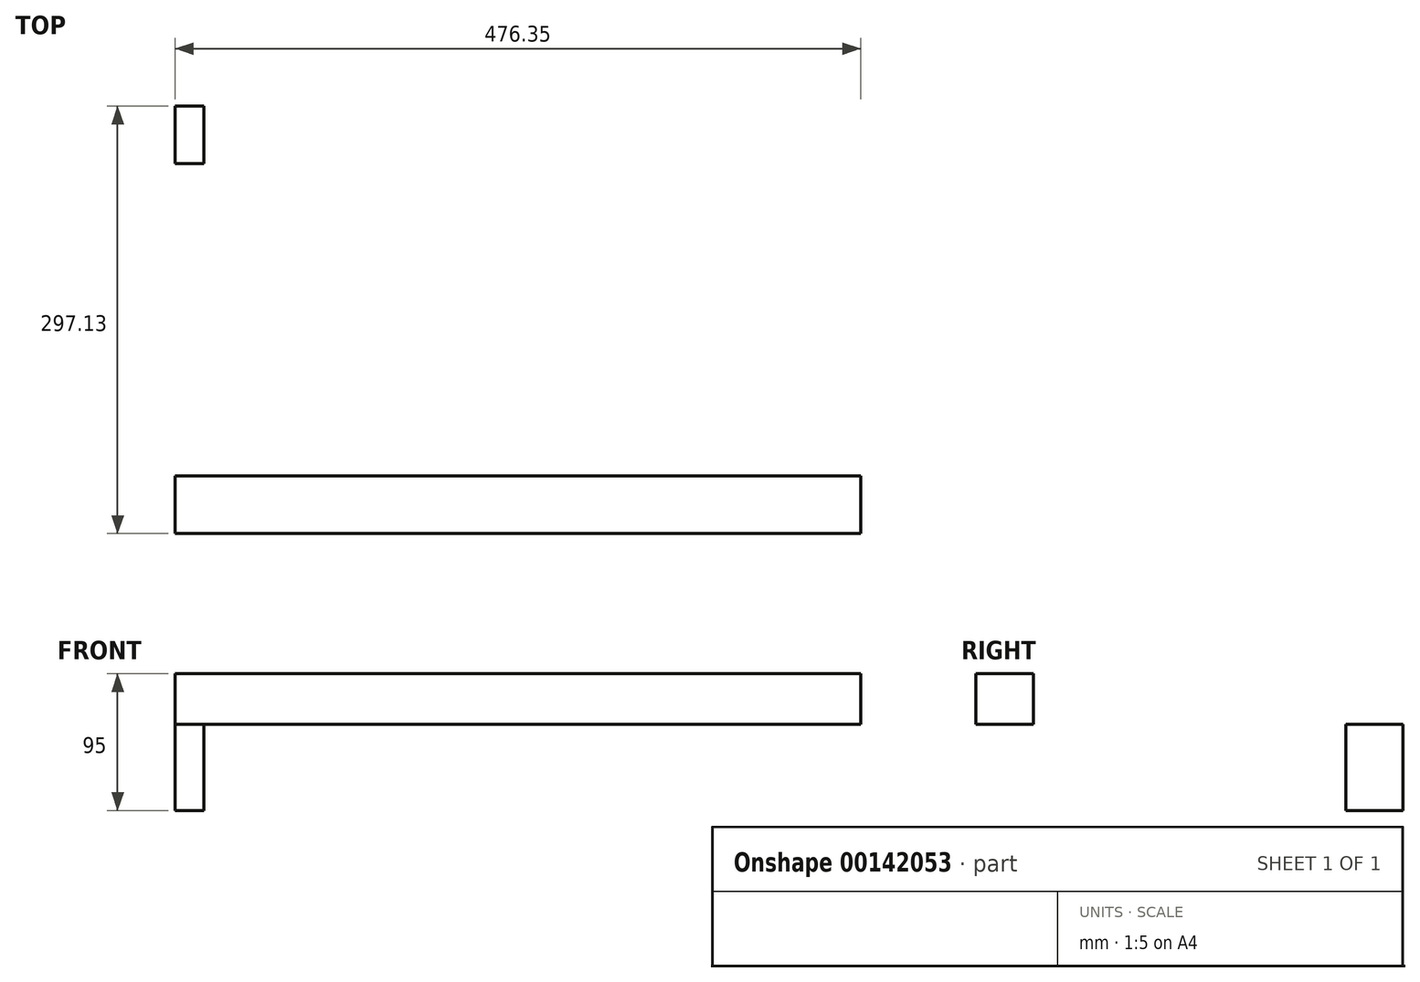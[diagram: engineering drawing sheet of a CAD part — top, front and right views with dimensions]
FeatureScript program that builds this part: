
annotation { "Feature Type Name" : "Feature", "Feature Type Description" : "" }
export const myFeature = defineFeature(function(context is Context, id is Id, definition is map)
    precondition{}
    {
        {
            var Q0;
            Q0=qCreatedBy(makeId("Top.planeOp"),FACE);
            var sketch = newSketch(context, id + "F0", { "sketchPlane" : qUnion([Q0])});
            skLineSegment(sketch, "E0.bottom", {"start": v(-127.44, 57.35) * mm, "end": v(172.56, 57.35) * mm});
            skLineSegment(sketch, "E0.top", {"start": v(-127.44, -142.65) * mm, "end": v(172.56, -142.65) * mm});
            skLineSegment(sketch, "E0.left", {"start": v(-127.44, 57.35) * mm, "end": v(-127.44, -142.65) * mm});
            skLineSegment(sketch, "E0.right", {"start": v(172.56, 57.35) * mm, "end": v(172.56, -142.65) * mm});
            skLineSegment(sketch, "E1.bottom", {"start": v(-236.3, 146.91) * mm, "end": v(253.7, 146.91) * mm});
            skLineSegment(sketch, "E1.top", {"start": v(-236.3, -253.09) * mm, "end": v(253.7, -253.09) * mm});
            skLineSegment(sketch, "E1.left", {"start": v(-236.3, 146.91) * mm, "end": v(-236.3, -253.09) * mm});
            skLineSegment(sketch, "E1.right", {"start": v(253.7, 146.91) * mm, "end": v(253.7, -253.09) * mm});
            skLineSegment(sketch, "E2.bottom", {"start": v(-156.3, 106.91) * mm, "end": v(193.7, 106.91) * mm});
            skLineSegment(sketch, "E2.top", {"start": v(-156.3, -193.09) * mm, "end": v(193.7, -193.09) * mm});
            skLineSegment(sketch, "E2.left", {"start": v(-156.3, 106.91) * mm, "end": v(-156.3, -193.09) * mm});
            skLineSegment(sketch, "E2.right", {"start": v(193.7, 106.91) * mm, "end": v(193.7, -193.09) * mm});
            skLineSegment(sketch, "E3.bottom", {"start": v(253.7, 106.91) * mm, "end": v(233.7, 106.91) * mm});
            skLineSegment(sketch, "E3.top", {"start": v(253.7, -213.09) * mm, "end": v(233.7, -213.09) * mm});
            skLineSegment(sketch, "E3.left", {"start": v(253.7, 106.91) * mm, "end": v(253.7, -213.09) * mm});
            skLineSegment(sketch, "E3.right", {"start": v(233.7, 106.91) * mm, "end": v(233.7, -213.09) * mm});
            skLineSegment(sketch, "E4.bottom", {"start": v(-236.3, 106.91) * mm, "end": v(-196.3, 106.91) * mm});
            skLineSegment(sketch, "E4.top", {"start": v(-236.3, -213.09) * mm, "end": v(-196.3, -213.09) * mm});
            skLineSegment(sketch, "E4.left", {"start": v(-236.3, 106.91) * mm, "end": v(-236.3, -213.09) * mm});
            skLineSegment(sketch, "E4.right", {"start": v(-196.3, 106.91) * mm, "end": v(-196.3, -213.09) * mm});
            skLineSegment(sketch, "E5.bottom", {"start": v(-236.3, -213.09) * mm, "end": v(-216.3, -213.09) * mm});
            skLineSegment(sketch, "E5.top", {"start": v(-236.3, -253.09) * mm, "end": v(-216.3, -253.09) * mm});
            skLineSegment(sketch, "E5.left", {"start": v(-236.3, -213.09) * mm, "end": v(-236.3, -253.09) * mm});
            skLineSegment(sketch, "E5.right", {"start": v(-216.3, -213.09) * mm, "end": v(-216.3, -253.09) * mm});
            skLineSegment(sketch, "E6.bottom", {"start": v(-236.3, 106.91) * mm, "end": v(-216.3, 106.91) * mm});
            skLineSegment(sketch, "E6.top", {"start": v(-236.3, 146.91) * mm, "end": v(-216.3, 146.91) * mm});
            skLineSegment(sketch, "E6.left", {"start": v(-236.3, 106.91) * mm, "end": v(-236.3, 146.91) * mm});
            skLineSegment(sketch, "E6.right", {"start": v(-216.3, 106.91) * mm, "end": v(-216.3, 146.91) * mm});
            skSolve(sketch);
        }
        {
            var Q0;
            {var subQ5=sQuery(id+"F0.wireOp",EDGE,"E1.bottom");Q0=makeQuery(id+"F0.imprint","IMPRINT",FACE,{"disambiguationData":[TD([[makeQuery(id+"F0.imprint","IMPRINT",EDGE,{"derivedFrom":subQ5}),-1.0]])]});}
            extrude(context, id + "F1", {"entities" : qUnion([Q0]), "depth" : 60 * mm});
        }
        {
            var Q0;
            Q0=makeQuery(id+"F1.opExtrude","CAP_FACE",FACE,{"disambiguationData":[OSD([sQuery(id+"F0.wireOp",EDGE,"E1.bottom"),sQuery(id+"F0.wireOp",EDGE,"E1.top"),sQuery(id+"F0.wireOp",EDGE,"E1.right"),sQuery(id+"F0.wireOp",EDGE,"E2.bottom"),sQuery(id+"F0.wireOp",EDGE,"E2.top"),sQuery(id+"F0.wireOp",EDGE,"E2.left"),sQuery(id+"F0.wireOp",EDGE,"E2.right"),sQuery(id+"F0.wireOp",EDGE,"E3.bottom"),sQuery(id+"F0.wireOp",EDGE,"E3.top"),sQuery(id+"F0.wireOp",EDGE,"E3.right"),sQuery(id+"F0.wireOp",EDGE,"E4.bottom"),sQuery(id+"F0.wireOp",EDGE,"E4.top"),sQuery(id+"F0.wireOp",EDGE,"E4.right"),sQuery(id+"F0.wireOp",EDGE,"E5.right"),sQuery(id+"F0.wireOp",EDGE,"E6.right")])],"isStart":false});
            var sketch = newSketch(context, id + "F2", { "sketchPlane" : qUnion([Q0])});
            skLineSegment(sketch, "E7.0.0", {"start": v(253.7, 146.91) * mm, "end": v(-216.3, 146.91) * mm});
            skLineSegment(sketch, "E7.0.1", {"start": v(-216.3, 146.91) * mm, "end": v(-216.3, 106.91) * mm});
            skLineSegment(sketch, "E7.0.2", {"start": v(-216.3, 106.91) * mm, "end": v(-196.3, 106.91) * mm});
            skLineSegment(sketch, "E7.0.3", {"start": v(-196.3, 106.91) * mm, "end": v(-196.3, -213.09) * mm});
            skLineSegment(sketch, "E7.0.4", {"start": v(-196.3, -213.09) * mm, "end": v(-216.3, -213.09) * mm});
            skLineSegment(sketch, "E7.0.5", {"start": v(-216.3, -213.09) * mm, "end": v(-216.3, -253.09) * mm});
            skLineSegment(sketch, "E7.0.6", {"start": v(-216.3, -253.09) * mm, "end": v(253.7, -253.09) * mm});
            skLineSegment(sketch, "E7.0.7", {"start": v(253.7, -253.09) * mm, "end": v(253.7, -213.09) * mm});
            skLineSegment(sketch, "E7.0.8", {"start": v(253.7, -213.09) * mm, "end": v(233.7, -213.09) * mm});
            skLineSegment(sketch, "E7.0.9", {"start": v(233.7, -213.09) * mm, "end": v(233.7, 106.91) * mm});
            skLineSegment(sketch, "E7.0.10", {"start": v(233.7, 106.91) * mm, "end": v(253.7, 106.91) * mm});
            skLineSegment(sketch, "E7.0.11", {"start": v(253.7, 106.91) * mm, "end": v(253.7, 146.91) * mm});
            skLineSegment(sketch, "E8.bottom", {"start": v(-236.3, -110.22) * mm, "end": v(240.05, -110.22) * mm});
            skLineSegment(sketch, "E8.top", {"start": v(-236.3, -150.22) * mm, "end": v(240.05, -150.22) * mm});
            skLineSegment(sketch, "E8.left", {"start": v(-236.3, -110.22) * mm, "end": v(-236.3, -150.22) * mm});
            skLineSegment(sketch, "E8.right", {"start": v(240.05, -110.22) * mm, "end": v(240.05, -150.22) * mm});
            skSolve(sketch);
        }
        {
            var Q0;
            {var subQ5=sQuery(id+"F2.wireOp",EDGE,"E8.left");Q0=makeQuery(id+"F2.imprint","IMPRINT",FACE,{"disambiguationData":[TD([[makeQuery(id+"F2.imprint","IMPRINT",EDGE,{"derivedFrom":subQ5}),1.0]])]});}
            var Q1;
            {var subQ0=sQuery(id+"F2.wireOp",EDGE,"E8.bottom");var subQ1=sQuery(id+"F2.wireOp",EDGE,"E7.0.3");var subQ2=makeQuery(id+"F2.imprint","INTERSECT",VERTEX,{"derivedFrom":[subQ1,subQ0]});Q1=makeQuery(id+"F2.imprint","IMPRINT",FACE,{"disambiguationData":[TD([[makeQuery(id+"F2.imprint","IMPRINT",EDGE,{"disambiguationData":[TD([[subQ2,-1.0]])],"derivedFrom":subQ1}),1.0]])]});}
            var Q2;
            {var subQ0=sQuery(id+"F2.wireOp",EDGE,"E8.bottom");var subQ1=makeQuery(id+"F1.opExtrude","CAP_EDGE",EDGE,{"disambiguationData":[OSD([sQuery(id+"F0.wireOp",EDGE,"E2.left")])],"isStart":false});var subQ2=makeQuery(id+"F2.imprint","INTERSECT",VERTEX,{"derivedFrom":[subQ1,subQ0]});Q2=makeQuery(id+"F2.imprint","IMPRINT",FACE,{"disambiguationData":[TD([[makeQuery(id+"F2.imprint","IMPRINT",EDGE,{"disambiguationData":[TD([[subQ2,-1.0]])],"derivedFrom":subQ0}),-1.0]])]});}
            var Q3;
            {var subQ0=sQuery(id+"F2.wireOp",EDGE,"E8.bottom");var subQ1=sQuery(id+"F2.wireOp",EDGE,"E7.0.9");var subQ2=makeQuery(id+"F2.imprint","INTERSECT",VERTEX,{"derivedFrom":[subQ1,subQ0]});Q3=makeQuery(id+"F2.imprint","IMPRINT",FACE,{"disambiguationData":[TD([[makeQuery(id+"F2.imprint","IMPRINT",EDGE,{"disambiguationData":[TD([[subQ2,-1.0]])],"derivedFrom":subQ1}),-1.0]])]});}
            var Q4;
            {var subQ5=sQuery(id+"F2.wireOp",EDGE,"E8.right");Q4=makeQuery(id+"F2.imprint","IMPRINT",FACE,{"disambiguationData":[TD([[makeQuery(id+"F2.imprint","IMPRINT",EDGE,{"derivedFrom":subQ5}),-1.0]])]});}
            extrude(context, id + "F3", {"entities" : qUnion([Q0, Q1, Q2, Q3, Q4]), "operationType" : NewBodyOperationType.ADD, "depth" : 95 * mm - 60 * mm});
        }
    });
